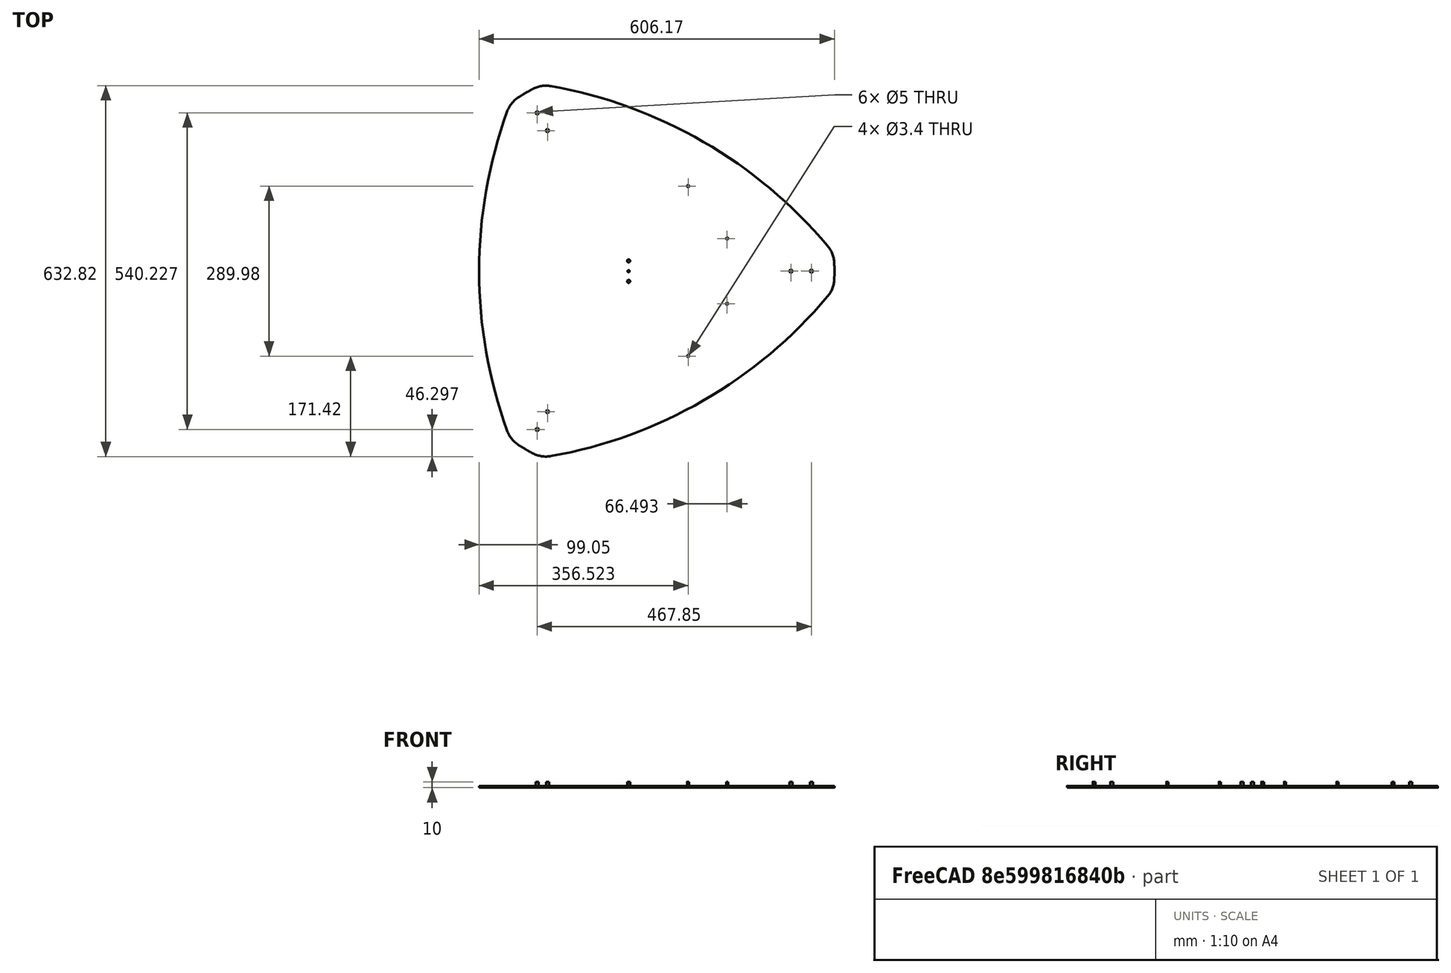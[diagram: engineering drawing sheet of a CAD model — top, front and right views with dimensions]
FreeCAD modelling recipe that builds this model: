
FCSTD DOCUMENT  (FreeCAD 1.1R38827 (Git))
Label: composit_stand3_basement_top_PP_model
License: All rights reserved
LicenseURL: http://en.wikipedia.org/wiki/All_rights_reserved
objects: Part::FeaturePython×7, App::Link×3, PartDesign::SubShapeBinder×2, PartDesign::CoordinateSystem×2, Part::Mirroring×1, Part::Compound×1, Part::Offset2D×1, PartDesign::Pad×1, Part::Cylinder×1, Part::Extrusion×1, Part::MultiFuse×1, PartDesign::Boolean×1, PartDesign::Body×1
note: 23 computed .brp shape members not serialized (recipe doc carries the construction recipe); baked Part::Feature solids carry a one-line shape summary decoded from their .brp
EXTERNAL_REF file=composit_stand3_basement_top_main.FCStd obj=Sketch
EXTERNAL_REF file=composit_stand3_basin_holder_main.FCStd obj=Join
EXTERNAL_REF file=../U-fix.FCStd obj=Sketch002
EXTERNAL_REF file=composit_stand3_base_part1_main.FCStd obj=Placment003

FEATURE [PartDesign::SubShapeBinder] Binder
  BindCopyOnChange = 0
  BindMode = 0
  ClaimChildren = true
  Fuse = false
  MakeFace = true
  OffsetFill = false
  OffsetIntersection = false
  OffsetJoinType = 0
  OffsetOpenResult = false
  PartialLoad = false
  Relative = true
  Support = -> [<external composit_stand3_basement_top_main.FCStd>#Sketch]
  _Version = 2
FEATURE [Part::FeaturePython] PolarArray  # WARN: FeaturePython — macro-defined, semantics opaque (R4)
  Alignment = 0
  AttacherType = Attacher::AttachEngine3D
  CellStart = A1
  Count = 3
  DistributionLaw = 0
  EndInclusive = false
  ExposePlacement = false
  FlipX = false
  FlipZ = false
  GeneratorMode = 0
  MarkerShape = 1
  MarkerSize = 0
  NumElements = 3
  OrientMode = 2
  Radius = 100
  Reverse = false
  SpanEnd = 360
  SpanStart = 0
  Step = 120
  Type = lattice2PolarArray2.PolarArray
  UseArcRadius = false
  UseArcRange = 0
  VSGVersion = 1
  Values = 0.0 | 120.0 | 240.0
  ValuesSource = 2
  isLattice = 1
FEATURE [Part::Mirroring] Part__Mirroring  label="Binder (Mirror #1)"
  Base = (0,0,0)
  Normal = (0,1,0)
  Source = -> Binder
FEATURE [Part::Compound] Compound
  Links = -> [Binder,Part__Mirroring]
FEATURE [Part::FeaturePython] Populate  label="Populate PolarArray with Compound"  # WARN: FeaturePython — macro-defined, semantics opaque (R4)
  Copying = 0
  ExposePlacement = false
  MarkerShape = 1
  MarkerSize = 0
  NumElements = 0
  Object = -> Compound
  OutputCompounding = 1
  PlacementsTo = -> PolarArray
  Referencing = 1
  Type = lattice2PopulateCopies.LatticePopulateCopies
  isLattice = 0
FEATURE [Part::FeaturePython] Connect  # WARN: FeaturePython — macro-defined, semantics opaque (R4)
  Objects = -> [Populate]
  Tolerance = 0
FEATURE [Part::Offset2D] Offset2D
  Fill = false
  Intersection = false
  Join = 0
  Mode = 1
  SelfIntersection = false
  Source = -> Connect
  Value = 2
FEATURE [PartDesign::SubShapeBinder] Binder001
  BindCopyOnChange = 0
  BindMode = 0
  ClaimChildren = true
  Context = -> Body [Binder001.]
  Fuse = false
  MakeFace = true
  OffsetFill = false
  OffsetIntersection = false
  OffsetJoinType = 0
  OffsetOpenResult = false
  PartialLoad = false
  Relative = true
  Support = -> [Offset2D]
  _Version = 2
FEATURE [PartDesign::Pad] Pad
  Direction = (0,0,1)
  Length = 3
  Length2 = 10
  Profile = -> Binder001
  Refine = true
  Suppressed = false
  Type = 0
FEATURE [Part::Cylinder] Cylinder  label="hole_3.4mm"
  Angle = 360
  AttacherType = Attacher::AttachEngine3D
  FirstAngle = 0
  Height = 10
  Radius = 1.7
  SecondAngle = 0
FEATURE [App::Link] Link  label="holes"
  LinkedObject = -> <external composit_stand3_basin_holder_main.FCStd>#Join
FEATURE [Part::FeaturePython] Populate001  label="Populate holes with hole_3.4mm"  # WARN: FeaturePython — macro-defined, semantics opaque (R4)
  Copying = 0
  ExposePlacement = false
  MarkerShape = 1
  MarkerSize = 0
  NumElements = 0
  Object = -> Cylinder
  OutputCompounding = 1
  PlacementsTo = -> Link
  Referencing = 0
  Type = lattice2PopulateCopies.LatticePopulateCopies
  isLattice = 0
FEATURE [PartDesign::CoordinateSystem] Local_CS  label="bottom_LCS"
  AttacherType = Attacher::AttachEngine3D
  AttachmentSupport = -> [XY_Plane]
  MapMode = 5
FEATURE [PartDesign::CoordinateSystem] Local_CS001  label="top_LCS"
  AttacherType = Attacher::AttachEngine3D
  AttachmentOffset = pos=(0,0,3) rot=(0,0,1;0rad)
  AttachmentSupport = -> [XY_Plane]
  MapMode = 5
  Placement = pos=(0,0,3) rot=(0,0,1;0rad)
FEATURE [App::Link] Link001  label="holes_bottom"
  LinkedObject = -> <external ../U-fix.FCStd>#Sketch002
FEATURE [Part::Extrusion] Extrude
  Base = -> Link001
  Dir = (0,0,1)
  DirMode = 2
  FaceMakerClass = Part::FaceMakerBullseye
  FaceMakerMode = 3
  LengthFwd = 10
  LengthRev = 0
  Solid = true
  Symmetric = false
FEATURE [App::Link] Link002  label="bottom_fix_placement"
  LinkTransform = true
  LinkedObject = -> <external composit_stand3_base_part1_main.FCStd>#Placment003
FEATURE [Part::FeaturePython] PolarArray001  # WARN: FeaturePython — macro-defined, semantics opaque (R4)
  Alignment = 0
  AttacherType = Attacher::AttachEngine3D
  CellStart = A1
  Count = 3
  DistributionLaw = 0
  EndInclusive = false
  ExposePlacement = false
  FlipX = false
  FlipZ = false
  GeneratorMode = 0
  MarkerShape = 1
  MarkerSize = 0
  NumElements = 3
  OrientMode = 2
  Radius = 250
  Reverse = false
  SpanEnd = 360
  SpanStart = 0
  Step = 120
  Type = lattice2PolarArray2.PolarArray
  UseArcRadius = false
  UseArcRange = 0
  VSGVersion = 1
  Values = 0.0 | 120.0 | 240.0
  ValuesSource = 2
  isLattice = 1
FEATURE [Part::FeaturePython] Populate002  label="Populate PolarArray001 with bottom_fix_placement"  # WARN: FeaturePython — macro-defined, semantics opaque (R4)
  Copying = 0
  ExposePlacement = false
  MarkerShape = 1
  MarkerSize = 0
  NumElements = 3
  Object = -> Link002
  OutputCompounding = 0
  PlacementsTo = -> PolarArray001
  Referencing = 1
  Type = lattice2PopulateCopies.LatticePopulateCopies
  isLattice = 1
FEATURE [Part::FeaturePython] Populate003  label="Populate Populate PolarArray001 with bottom_fix_placement with Extrude"  # WARN: FeaturePython — macro-defined, semantics opaque (R4)
  Copying = 0
  ExposePlacement = false
  MarkerShape = 1
  MarkerSize = 0
  NumElements = 0
  Object = -> Extrude
  OutputCompounding = 1
  PlacementsTo = -> Populate002
  Referencing = 0
  Type = lattice2PopulateCopies.LatticePopulateCopies
  isLattice = 0
FEATURE [Part::MultiFuse] Fusion
  Shapes = -> [Populate001,Populate003]
FEATURE [PartDesign::Boolean] Boolean
  BaseFeature = -> Pad
  Group = -> [Fusion]
  Suppressed = false
  Type = 1
  UsePlacement = true
FEATURE [PartDesign::Body] Body  label="top_PP"
  AllowCompound = false
  Group = -> [Binder001,Pad,Boolean,Local_CS,Local_CS001]
  Origin = -> Origin
  Tip = -> Boolean

RESOLVED EXTERNAL PARTS (link-assembly join: the EXTERNAL_REF files above that resolve inside this repo's crawl, each included once):
---- part ../U-fix.FCStd = doc fcstd_8b42821c5992 ----
FCSTD DOCUMENT  (FreeCAD 1.1R38827 (Git))
Label: U-fix
License: All rights reserved
LicenseURL: http://en.wikipedia.org/wiki/All_rights_reserved
objects: Sketcher::SketchObject×7, TechDraw::DrawViewDimension×4, TechDraw::DrawViewPart×3, PartDesign::SubShapeBinder×2, PartDesign::Pocket×2, PartDesign::FeaturePython×1, PartDesign::Mirrored×1, TechDraw::DrawSVGTemplate×1, Part::Feature×1, PartDesign::Hole×1, PartDesign::Body×1, TechDraw::DrawPage×1, App::DocumentObjectGroup×1
note: 37 computed .brp shape members not serialized (recipe doc carries the construction recipe); baked Part::Feature solids carry a one-line shape summary decoded from their .brp
EXTERNAL_REF file=ugol90degX40mm.FCStd obj=Binder002
EXTERNAL_REF file=wheel50mm.FCStd obj=Populate001

FEATURE [Sketcher::SketchObject] Sketch
  ArcFitTolerance = 0
  AttachmentSupport = -> [XZ_Plane]
  FullyConstrained = true
  MakeInternals = false
  MapMode = 5
  Placement = pos=(0,0,0) rot=(1,0,0;1.5708rad)
  sketch-geometry (5):
    g0: LineSegment StartX=-11.5 StartY=16 StartZ=0 EndX=-11.5 EndY=0 EndZ=0
    g1: LineSegment StartX=-11.5 StartY=0 StartZ=0 EndX=11.5 EndY=0 EndZ=0
    g2: LineSegment StartX=11.5 StartY=0 StartZ=0 EndX=11.5 EndY=16 EndZ=0
    g3: LineSegment [constr] StartX=11.5 StartY=16 StartZ=0 EndX=-11.5 EndY=16 EndZ=0
    g4: GeomPoint [constr] X=0 Y=8 Z=0
  constraints (13):
    c: Coincident(g0,g1)
    c: Coincident(g1,g2)
    c: Coincident(g2,g3)
    c: Coincident(g3,g0)
    c: Horizontal(g1)
    c: Horizontal(g3)
    c: Vertical(g0)
    c: Vertical(g2)
    c: Symmetric(g1,g0,g4)
    c: PointOnObject(g4,g-2)
    c: PointOnObject(g1,g-1)
    c: DistanceX(g1,g1) = 23  'width'
    c: DistanceY(g2) = 16  'height'
FEATURE [PartDesign::FeaturePython] BaseBend  # WARN: FeaturePython — macro-defined, semantics opaque (R4)
  BendSide = 1
  BendSketch = -> Sketch
  MidPlane = true
  Reverse = false
  Suppressed = false
  length = 65
  radius = 2
  thickness = 1
FEATURE [PartDesign::SubShapeBinder] Binder  label="U-fix_vert_holes"
  BindCopyOnChange = 0
  BindMode = 0
  ClaimChildren = false
  Context = -> Body [Binder.]
  Fuse = false
  MakeFace = true
  OffsetFill = false
  OffsetIntersection = false
  OffsetJoinType = 0
  OffsetOpenResult = false
  PartialLoad = false
  Placement = pos=(0,0,0) rot=(0,0,1;1.5708rad)
  Relative = true
  Support = -> [<external ugol90degX40mm.FCStd>#Binder002]
  _Version = 2
  expr: Support = <<ugol90degX40mm>>#<<vert>>._self
FEATURE [PartDesign::Pocket] Pocket
  BaseFeature = -> BaseBend
  Direction = (1,-2e-16,0)
  Length = 5
  Length2 = 5
  Midplane = true
  Profile = -> Binder
  Suppressed = false
  Type = 1
FEATURE [Sketcher::SketchObject] Sketch001
  ArcFitTolerance = 0
  AttachmentOffset = pos=(32.5,16,0) rot=(0,0,1;0rad)
  AttachmentSupport = -> [YZ_Plane]
  FullyConstrained = true
  MakeInternals = false
  MapMode = 5
  Placement = pos=(0,32.5,16) rot=(0.57735,0.57735,0.57735;2.0944rad)
  expr: .AttachmentOffset.Base.x = BaseBend.length / 2
  expr: .AttachmentOffset.Base.y = Sketch.Constraints.height
  sketch-geometry (3):
    g0: ArcOfCircle CenterX=-5 CenterY=-5 CenterZ=0 NormalX=0 NormalY=0 NormalZ=1 AngleXU=0 Radius=5 StartAngle=0 EndAngle=1.5708
    g1: LineSegment StartX=-9e-16 StartY=-5 StartZ=0 EndX=0 EndY=0 EndZ=0
    g2: LineSegment StartX=0 StartY=0 StartZ=0 EndX=-5.00003 EndY=-4.65468e-11 EndZ=0
  constraints (8):
    c: PointOnObject(g0,g-1)
    c: PointOnObject(g0,g-2)
    c: Coincident(g1,g2)
    c: Coincident(g2,g0)
    c: Tangent(g2,g0)
    c: Tangent(g0,g1) = -1.5708
    c: Coincident(g1,g-1)
    c: Diameter(g0) = 10
FEATURE [PartDesign::Pocket] Pocket001
  BaseFeature = -> Pocket
  Direction = (-1,0,0)
  Length = 5
  Length2 = 5
  Midplane = true
  Profile = -> Sketch001
  ReferenceAxis = -> Sketch001 [N_Axis]
  Suppressed = false
  Type = 1
FEATURE [PartDesign::Mirrored] Mirrored
  BaseFeature = -> Pocket001
  MirrorPlane = -> XZ_Plane
  Originals = -> [Pocket001]
  Suppressed = false
  TransformMode = 0
FEATURE [Sketcher::SketchObject] Sketch002  label="holes_bottom"
  ArcFitTolerance = 0
  AttachmentSupport = -> [XY_Plane]
  FullyConstrained = true
  MakeInternals = false
  MapMode = 5
  sketch-geometry (2):
    g0: Circle CenterX=0 CenterY=17.5 CenterZ=0 NormalX=0 NormalY=0 NormalZ=1 AngleXU=0 Radius=2.5
    g1: Circle CenterX=0 CenterY=-17.5 CenterZ=0 NormalX=0 NormalY=0 NormalZ=1 AngleXU=0 Radius=2.5
  constraints (5):
    c: PointOnObject(g0,g-2)
    c: Symmetric(g1,g0,g-1)
    c: Equal(g1,g0)
    c: Diameter(g1) = 5
    c: DistanceY(g1,g0) = 35
FEATURE [TechDraw::DrawSVGTemplate] Template
  Height = 210
  Orientation = 1
  Template = <path>
  Width = 297
FEATURE [Part::Feature] Unfold
  Placement = pos=(0,0,0) rot=(0,0,1;1.5708rad)
  shape: bbox 53 x 50.85 x 1 mm, 16 faces (baked)
FEATURE [Sketcher::SketchObject] Unfold_Sketch_Outline
  ArcFitTolerance = 0
  FullyConstrained = false
  MakeInternals = false
  sketch-geometry (8):
    g0: ArcOfCircle CenterX=21.5 CenterY=-20.427 CenterZ=0 NormalX=0 NormalY=0 NormalZ=1 AngleXU=4e-16 Radius=5 StartAngle=4.71238 EndAngle=6.28319
    g1: LineSegment StartX=26.5 StartY=20.427 StartZ=0 EndX=26.5 EndY=-20.427 EndZ=0
    g2: ArcOfCircle CenterX=21.5 CenterY=20.427 CenterZ=0 NormalX=0 NormalY=0 NormalZ=1 AngleXU=-4e-16 Radius=5 StartAngle=0 EndAngle=1.5708
    g3: LineSegment StartX=21.5 StartY=25.427 StartZ=0 EndX=-21.5 EndY=25.427 EndZ=0
    g4: ArcOfCircle CenterX=-21.5 CenterY=20.427 CenterZ=0 NormalX=0 NormalY=0 NormalZ=1 AngleXU=-3.14159 Radius=5 StartAngle=4.71238 EndAngle=6.28319
    g5: LineSegment StartX=-26.5 StartY=20.427 StartZ=0 EndX=-26.5 EndY=-20.427 EndZ=0
    g6: ArcOfCircle CenterX=-21.5 CenterY=-20.427 CenterZ=0 NormalX=0 NormalY=0 NormalZ=1 AngleXU=3.14159 Radius=5 StartAngle=0 EndAngle=1.5708
    g7: LineSegment StartX=21.5 StartY=-25.427 StartZ=0 EndX=-21.5 EndY=-25.427 EndZ=0
FEATURE [Sketcher::SketchObject] Unfold_Sketch_Internal
  ArcFitTolerance = 0
  FullyConstrained = false
  MakeInternals = false
  sketch-geometry (6):
    g0: Circle CenterX=17.5 CenterY=0 CenterZ=0 NormalX=0 NormalY=0 NormalZ=1 AngleXU=1.5708 Radius=2.75
    g1: Circle CenterX=-17.5 CenterY=0 CenterZ=0 NormalX=0 NormalY=0 NormalZ=1 AngleXU=1.5708 Radius=2.75
    g2: Circle CenterX=20 CenterY=-19.927 CenterZ=0 NormalX=0 NormalY=0 NormalZ=1 AngleXU=2e-16 Radius=1.7
    g3: Circle CenterX=-20 CenterY=-19.927 CenterZ=0 NormalX=0 NormalY=0 NormalZ=1 AngleXU=2e-16 Radius=1.7
    g4: Circle CenterX=20 CenterY=19.927 CenterZ=0 NormalX=0 NormalY=0 NormalZ=-1 AngleXU=-3.14159 Radius=1.7
    g5: Circle CenterX=-20 CenterY=19.927 CenterZ=0 NormalX=0 NormalY=0 NormalZ=-1 AngleXU=-3.14159 Radius=1.7
FEATURE [Sketcher::SketchObject] Unfold_Sketch_bends
  ArcFitTolerance = 0
  FullyConstrained = false
  MakeInternals = false
  sketch-geometry (2):
    g0: LineSegment StartX=-26.5 StartY=10.4635 StartZ=0 EndX=26.5 EndY=10.4635 EndZ=0
    g1: LineSegment StartX=-26.5 StartY=-10.4635 StartZ=0 EndX=26.5 EndY=-10.4635 EndZ=0
FEATURE [Sketcher::SketchObject] Unfold_Sketch
  ArcFitTolerance = 0
  ExternalGeometry = -> [Unfold_Sketch_bends]
  FullyConstrained = false
  MakeInternals = false
  sketch-geometry (18):
    g0: ArcOfCircle CenterX=21.5 CenterY=-20.427 CenterZ=0 NormalX=0 NormalY=0 NormalZ=1 AngleXU=4e-16 Radius=5 StartAngle=4.71238 EndAngle=6.28319
    g1: LineSegment StartX=21.5 StartY=-25.427 StartZ=0 EndX=-21.5 EndY=-25.427 EndZ=0
    g2: ArcOfCircle CenterX=-21.5 CenterY=-20.427 CenterZ=0 NormalX=0 NormalY=0 NormalZ=1 AngleXU=3.14159 Radius=5 StartAngle=0 EndAngle=1.5708
    g3: ArcOfCircle CenterX=-21.5 CenterY=20.427 CenterZ=0 NormalX=0 NormalY=0 NormalZ=1 AngleXU=-3.14159 Radius=5 StartAngle=4.71238 EndAngle=6.28319
    g4: LineSegment StartX=21.5 StartY=25.427 StartZ=0 EndX=-21.5 EndY=25.427 EndZ=0
    g5: ArcOfCircle CenterX=21.5 CenterY=20.427 CenterZ=0 NormalX=0 NormalY=0 NormalZ=1 AngleXU=-4e-16 Radius=5 StartAngle=0 EndAngle=1.5708
    g6: Circle CenterX=-17.5 CenterY=0 CenterZ=0 NormalX=0 NormalY=0 NormalZ=1 AngleXU=1.5708 Radius=2.75
    g7: Circle CenterX=17.5 CenterY=0 CenterZ=0 NormalX=0 NormalY=0 NormalZ=1 AngleXU=1.5708 Radius=2.75
    g8: Circle CenterX=-20 CenterY=19.927 CenterZ=0 NormalX=0 NormalY=0 NormalZ=-1 AngleXU=-3.14159 Radius=1.7
    g9: Circle CenterX=20 CenterY=19.927 CenterZ=0 NormalX=0 NormalY=0 NormalZ=-1 AngleXU=-3.14159 Radius=1.7
    g10: Circle CenterX=-20 CenterY=-19.927 CenterZ=0 NormalX=0 NormalY=0 NormalZ=1 AngleXU=2e-16 Radius=1.7
    g11: Circle CenterX=20 CenterY=-19.927 CenterZ=0 NormalX=0 NormalY=0 NormalZ=1 AngleXU=2e-16 Radius=1.7
    g12: LineSegment StartX=26.5 StartY=20.427 StartZ=0 EndX=26.5 EndY=-20.427 EndZ=0
    g13: LineSegment StartX=-26.5 StartY=20.427 StartZ=0 EndX=-26.5 EndY=-20.427 EndZ=0
    g14: LineSegment StartX=26.5 StartY=-10.4635 StartZ=0 EndX=24.5 EndY=-10.4635 EndZ=0
    g15: LineSegment StartX=26.5 StartY=10.4635 StartZ=0 EndX=24.5 EndY=10.4635 EndZ=0
    g16: LineSegment StartX=-26.5 StartY=10.4635 StartZ=0 EndX=-24.5 EndY=10.4635 EndZ=0
    g17: LineSegment StartX=-26.5 StartY=-10.4635 StartZ=0 EndX=-24.5 EndY=-10.4635 EndZ=0
  constraints (20):
    c: Coincident(g2,g13)
    c: Coincident(g3,g13)
    c: Coincident(g1,g2)
    c: Coincident(g3,g4)
    c: Coincident(g0,g1)
    c: Coincident(g4,g5)
    c: Coincident(g0,g12)
    c: Coincident(g5,g12)
    c: Coincident(g14,g-4)
    c: Coincident(g15,g-3)
    c: Coincident(g16,g-3)
    c: Coincident(g17,g-4)
    c: PointOnObject(g17,g-4)
    c: PointOnObject(g16,g-3)
    c: PointOnObject(g15,g-3)
    c: PointOnObject(g14,g-4)
    c: Equal(g14,g15)
    c: Equal(g15,g16)
    c: Equal(g16,g17)
    c: Distance(g17) = 2
FEATURE [PartDesign::SubShapeBinder] Binder001
  BindCopyOnChange = 0
  BindMode = 0
  ClaimChildren = false
  Context = -> Body [Binder001.]
  Fuse = false
  MakeFace = true
  OffsetFill = false
  OffsetIntersection = false
  OffsetJoinType = 0
  OffsetOpenResult = false
  PartialLoad = false
  Placement = pos=(0,0,0) rot=(0,0,1;0.785398rad)
  Relative = true
  Support = -> [<external wheel50mm.FCStd>#Populate001]
  _Version = 2
  expr: Support = wheel50mm#<<holes_max>>._self
FEATURE [PartDesign::Hole] Hole
  BaseFeature = -> Mirrored
  CustomThreadClearance = 0
  Depth = 25
  DepthType = 0
  Diameter = 5.5
  DrillForDepth = false
  DrillPoint = 1
  DrillPointAngle = 118
  HoleCutCountersinkAngle = 90
  HoleCutCustomValues = false
  HoleCutDepth = 0
  HoleCutDiameter = 6.1
  HoleCutType = 0
  ModelThread = false
  Profile = -> Binder001
  Reversed = true
  Suppressed = false
  Tapered = false
  TaperedAngle = 90
  ThreadClass = 0
  ThreadDepth = 25
  ThreadDepthType = 0
  ThreadDirection = 0
  ThreadFit = 0
  ThreadSize = 0
  ThreadType = 0
  Threaded = false
  UseCustomThreadClearance = false
FEATURE [PartDesign::Body] Body  label="U_fix_material_0.50ansi"
  AllowCompound = false
  Group = -> [Sketch,BaseBend,Binder,Pocket,Sketch001,Pocket001,Mirrored,Sketch002,Hole,Binder001]
  Origin = -> Origin
  Tip = -> Hole
FEATURE [TechDraw::DrawViewPart] View
  CoarseView = false
  Direction = (0,-1,0)
  Focus = 100
  HardHidden = false
  IsoCount = 0
  IsoHidden = false
  IsoVisible = false
  LockPosition = false
  Perspective = false
  Rotation = 0
  ScaleType = 0
  ScrubCount = 0
  SeamHidden = false
  SeamVisible = true
  SmoothHidden = false
  SmoothVisible = true
  Source = -> [Body]
  X = 69.5
  XDirection = (1,0,0)
  Y = 105
  expr: Y = Template.Height / 2
FEATURE [TechDraw::DrawViewPart] View001
  CoarseView = false
  Direction = (1,0,0)
  Focus = 100
  HardHidden = false
  IsoCount = 0
  IsoHidden = false
  IsoVisible = false
  LockPosition = false
  Perspective = false
  Rotation = 0
  ScaleType = 0
  ScrubCount = 0
  SeamHidden = false
  SeamVisible = true
  SmoothHidden = false
  SmoothVisible = true
  Source = -> [Body]
  X = 226.5
  XDirection = (0,1,-1.19209e-07)
  Y = 105
  expr: Y = Template.Height / 2
FEATURE [TechDraw::DrawViewPart] View002
  CoarseView = false
  Direction = (0,0,1)
  Focus = 100
  HardHidden = false
  IsoCount = 0
  IsoHidden = false
  IsoVisible = false
  LockPosition = false
  Perspective = false
  Rotation = 0
  ScaleType = 0
  ScrubCount = 0
  SeamHidden = false
  SeamVisible = true
  SmoothHidden = false
  SmoothVisible = true
  Source = -> [Body]
  X = 148.5
  XDirection = (1,0,0)
  Y = 105
  expr: Y = Template.Height / 2
FEATURE [TechDraw::DrawViewDimension] Dimension004
  AngleOverride = false
  Arbitrary = false
  ArbitraryTolerances = false
  EqualTolerance = true
  ExtensionAngle = 0
  FormatSpec = R%.2w
  FormatSpecOverTolerance = %+.2w
  FormatSpecUnderTolerance = %+.2w
  Inverted = false
  LineAngle = 0
  LockPosition = false
  MeasureType = 1
  OverTolerance = 0
  References2D = -> [View]
  Rotation = 0
  ScaleType = 0
  TheoreticalExact = false
  Type = 4
  UnderTolerance = 0
  X = -23.1952
  Y = -5.48414
FEATURE [TechDraw::DrawViewDimension] Dimension005
  AngleOverride = false
  Arbitrary = false
  ArbitraryTolerances = false
  EqualTolerance = true
  ExtensionAngle = 0
  FormatSpec = R%.2w
  FormatSpecOverTolerance = %+.2w
  FormatSpecUnderTolerance = %+.2w
  Inverted = false
  LineAngle = 0
  LockPosition = false
  MeasureType = 1
  OverTolerance = 0
  References2D = -> [View]
  Rotation = 0
  ScaleType = 0
  TheoreticalExact = false
  Type = 4
  UnderTolerance = 0
  X = 1.1181
  Y = 3.75976
FEATURE [TechDraw::DrawViewDimension] Dimension
  AngleOverride = false
  Arbitrary = false
  ArbitraryTolerances = false
  BoxCorners = (2) [(-11.5,-8,-1e-07),(11.5,8,1e-07)]
  EqualTolerance = true
  ExtensionAngle = 0
  FormatSpec = %.2w
  FormatSpecOverTolerance = %+.2w
  FormatSpecUnderTolerance = %+.2w
  Inverted = false
  LineAngle = 0
  LockPosition = false
  MeasureType = 1
  OverTolerance = 0
  References2D = -> [View]
  Rotation = 0
  ScaleType = 0
  TheoreticalExact = false
  Type = 1
  UnderTolerance = 0
  X = -0.401552
  Y = 25.4578
FEATURE [TechDraw::DrawViewDimension] Dimension006
  AngleOverride = false
  Arbitrary = false
  ArbitraryTolerances = false
  BoxCorners = (2) [(-11.5,-8,-1e-07),(11.5,8,1e-07)]
  EqualTolerance = true
  ExtensionAngle = 0
  FormatSpec = %.2w
  FormatSpecOverTolerance = %+.2w
  FormatSpecUnderTolerance = %+.2w
  Inverted = false
  LineAngle = 0
  LockPosition = false
  MeasureType = 1
  OverTolerance = 0
  References2D = -> [View]
  Rotation = 0
  ScaleType = 0
  TheoreticalExact = false
  Type = 2
  UnderTolerance = 0
  X = 18.6275
  Y = 2.60039
FEATURE [TechDraw::DrawPage] Page
  KeepUpdated = true
  NextBalloonIndex = 1
  ProjectionType = 0
  Template = -> Template
  Views = -> [View,View001,View002,Dimension004,Dimension005,Dimension,Dimension006]
FEATURE [App::DocumentObjectGroup] Group  label="unfold_Group"
  Group = -> [Page,Unfold,Unfold_Sketch,Unfold_Sketch_Outline,Unfold_Sketch_Internal,Unfold_Sketch_bends]
note: 1 file-system path scrubbed to <path> (originals preserved in the JSON sidecar)
---- part composit_stand3_base_part1_main.FCStd = doc fcstd_83d21d27950e ----
FCSTD DOCUMENT  (FreeCAD 1.1R38827 (Git))
Label: composit_stand3_base_part1_main
License: All rights reserved
LicenseURL: http://en.wikipedia.org/wiki/All_rights_reserved
objects: Part::FeaturePython×32, Sketcher::SketchObject×7, App::Link×5, Part::Extrusion×3, PartDesign::SubShapeBinder×2, Part::MultiFuse×1, Part::Feature×1
note: 53 computed .brp shape members not serialized (recipe doc carries the construction recipe); baked Part::Feature solids carry a one-line shape summary decoded from their .brp
EXTERNAL_REF file=composit_stand3_main.FCStd obj=Sketch
EXTERNAL_REF file=composit_stand3_main.FCStd obj=LinearArray
EXTERNAL_REF file=../module.FCStd obj=Sketch
EXTERNAL_REF file=composit_stand3_sink_main.FCStd obj=Sketch001
EXTERNAL_REF file=composit_stand3_bottom_shield_main.FCStd obj=Placment
EXTERNAL_REF file=composit_stand3_bottom_shield_main.FCStd obj=LinearArray
EXTERNAL_REF file=composit_stand3_sink_main.FCStd obj=Sketch005

FEATURE [PartDesign::SubShapeBinder] Binder
  BindCopyOnChange = 0
  BindMode = 0
  ClaimChildren = true
  Fuse = false
  MakeFace = false
  OffsetFill = false
  OffsetIntersection = false
  OffsetJoinType = 0
  OffsetOpenResult = false
  PartialLoad = false
  Relative = false
  Support = -> [<external composit_stand3_main.FCStd>#Sketch]
  _Version = 2
FEATURE [Sketcher::SketchObject] Sketch
  ArcFitTolerance = 0
  ExternalGeometry = -> [Binder]
  FullyConstrained = true
  MakeInternals = false
  sketch-geometry (2):
    g0: LineSegment StartX=8.37158 StartY=14.5 StartZ=0 EndX=4.90748 EndY=14.5 EndZ=0
    g1: LineSegment StartX=4.90748 StartY=14.5 StartZ=0 EndX=-2.59252 EndY=27.4904 EndZ=0
  constraints (7):
    c: Horizontal(g0)
    c: Coincident(g0,g1)
    c: Angle(g1) = 2.0944
    c: Coincident(g0,g-3)
    c: Distance(g0,g1) = 3
    c: Distance(g1) = 15
    c: DistanceX(g0) = 4.90748  'x_offset'
FEATURE [Part::FeaturePython] LinearArray  # WARN: FeaturePython — macro-defined, semantics opaque (R4)
  Alignment = 0
  CellStart = A1
  Count = 11
  Dir = (0,0,-1)
  DirIsDriven = true
  DistributionLaw = 0
  DrivenProperty = 1
  EndInclusive = true
  ExposePlacement = false
  GeneratorMode = 1
  MarkerShape = 1
  MarkerSize = 0
  NumElements = 11
  OrientMode = 0
  Point = (0,0,0)
  PointIsDriven = true
  Reverse = false
  SpanEnd = 827
  SpanStart = 27
  Step = 80
  Type = lattice2LinearArray.LinearArray
  VSGVersion = 1
  Values = 27.0 | 107.0 | 187.0 | 267.0 | 347.0 | 427.0 | 507.0 | 587.0 | 667.0 | 747.0 | 827.0
  ValuesSource = 2
  isLattice = 1
  expr: SpanEnd = Step * (Count - 1) * 1 mm + SpanStart
FEATURE [App::Link] Link  label="modules_placement_x"
  LinkTransform = true
  LinkedObject = -> <external composit_stand3_main.FCStd>#LinearArray
FEATURE [Part::FeaturePython] Placment  label="top_placement"  # WARN: FeaturePython — macro-defined, semantics opaque (R4)
  AttacherType = Attacher::AttachEngine3D
  ExposePlacement = true
  MarkerShape = 1
  MarkerSize = 200
  NumElements = 1
  Placement = pos=(0,0,1428) rot=(0,0,1;0rad)
  Type = lattice2AttachablePlacement.AttachablePlacement
  isLattice = 1
FEATURE [Part::FeaturePython] Populate  label="Populate modules_placement_x with LinearArray"  # WARN: FeaturePython — macro-defined, semantics opaque (R4)
  Copying = 0
  ExposePlacement = false
  MarkerShape = 1
  MarkerSize = 0
  NumElements = 22
  Object = -> LinearArray
  OutputCompounding = 0
  PlacementsTo = -> Link
  Referencing = 0
  Type = lattice2PopulateCopies.LatticePopulateCopies
  isLattice = 1
FEATURE [Part::FeaturePython] Populate001  label="Populate Placment with Populate modules_placement_x with LinearArray"  # WARN: FeaturePython — macro-defined, semantics opaque (R4)
  Copying = 0
  ExposePlacement = false
  MarkerShape = 1
  MarkerSize = 0
  NumElements = 22
  Object = -> Populate
  OutputCompounding = 0
  PlacementsTo = -> Placment
  Referencing = 0
  Type = lattice2PopulateCopies.LatticePopulateCopies
  isLattice = 1
FEATURE [Part::FeaturePython] Placment001  # WARN: FeaturePython — macro-defined, semantics opaque (R4)
  AttacherType = Attacher::AttachEngine3D
  ExposePlacement = true
  MarkerShape = 1
  MarkerSize = 50
  NumElements = 1
  Placement = pos=(0,0,0) rot=(0,0.707107,0.707107;3.14159rad)
  Type = lattice2AttachablePlacement.AttachablePlacement
  isLattice = 1
FEATURE [Part::FeaturePython] Populate002  label="Populate Populate Placment with Populate modules_placement_x with LinearArray with Placment001"  # WARN: FeaturePython — macro-defined, semantics opaque (R4)
  Copying = 0
  ExposePlacement = false
  MarkerShape = 1
  MarkerSize = 0
  NumElements = 22
  Object = -> Placment001
  OutputCompounding = 0
  PlacementsTo = -> Populate001
  Referencing = 0
  Type = lattice2PopulateCopies.LatticePopulateCopies
  isLattice = 1
FEATURE [Part::FeaturePython] Placment002  label="sink_placement"  # WARN: FeaturePython — macro-defined, semantics opaque (R4)
  AttacherType = Attacher::AttachEngine3D
  ExposePlacement = true
  MarkerShape = 1
  MarkerSize = 50
  NumElements = 1
  Placement = pos=(8.37158,14.5,410) rot=(0,0,1;1.0472rad)
  Type = lattice2AttachablePlacement.AttachablePlacement
  isLattice = 1
  expr: .Placement.Base.x = <<composit_stand3_main>>#<<main_sketch>>.Constraints.end_width / 2 / tan(60)
  expr: .Placement.Base.y = <<composit_stand3_main>>#<<main_sketch>>.Constraints.end_width / 2
FEATURE [App::Link] Link001  label="module_holes"
  LinkedObject = -> <external ../module.FCStd>#Sketch
FEATURE [Sketcher::SketchObject] Sketch001  label="basin_cut_top_sketch"
  ArcFitTolerance = 0
  FullyConstrained = true
  MakeInternals = false
  Placement = pos=(0,0,400) rot=(1,0,0;1.5708rad)
  expr: .Placement.Base.z = <<basin_cut_sketch>>.Constraints.height
  expr: Constraints[26] = <<basin_cut_sketch>>.Constraints.length
  expr: Constraints[28] = <<composit_stand3_main>>#<<main_sketch>>.Constraints.x_face_offset + 0.5 mm
  expr: Constraints[30] = <<composit_stand3_sink_main>>#<<side_bottom_edge>>.Constraints.angle
  sketch-geometry (14):
    g0: ArcOfEllipse CenterX=8.87158 CenterY=5 CenterZ=0 NormalX=0 NormalY=0 NormalZ=1 MajorRadius=40 MinorRadius=15 AngleXU=1.5708 StartAngle=4.71239 EndAngle=6.28319
    g1: LineSegment [constr] StartX=8.87158 StartY=45 StartZ=0 EndX=8.87158 EndY=-35 EndZ=0
    g2: LineSegment [constr] StartX=-6.12842 StartY=5 StartZ=0 EndX=23.8716 EndY=5 EndZ=0
    g3: GeomPoint [constr] X=8.87158 Y=42.081 Z=0
    g4: GeomPoint [constr] X=8.87158 Y=-32.081 Z=0
    g5: ArcOfCircle CenterX=28.8716 CenterY=5 CenterZ=0 NormalX=0 NormalY=0 NormalZ=1 AngleXU=0 Radius=5 StartAngle=3.14159 EndAngle=4.71239
    g6: LineSegment StartX=28.8716 StartY=0 StartZ=0 EndX=0 EndY=0 EndZ=0
    g7: LineSegment StartX=0 StartY=0 StartZ=0 EndX=0 EndY=45 EndZ=0
    g8: LineSegment StartX=0 StartY=45 StartZ=0 EndX=8.87158 EndY=45 EndZ=0
    g9: LineSegment StartX=238.446 StartY=3.98838 StartZ=0 EndX=238.446 EndY=0 EndZ=0
    g10: LineSegment StartX=238.446 StartY=0 StartZ=0 EndX=170.25 EndY=0 EndZ=0
    g11: LineSegment StartX=170.836 StartY=0.0172058 StartZ=0 EndX=238.446 EndY=3.98838 EndZ=0
    g12: ArcOfCircle CenterX=170.25 CenterY=10 CenterZ=0 NormalX=0 NormalY=0 NormalZ=1 AngleXU=0 Radius=10 StartAngle=4.71239 EndAngle=4.77106
    g13: LineSegment [constr] StartX=0 StartY=0 StartZ=0 EndX=238.446 EndY=14.0056 EndZ=0
  constraints (31):
    c: InternalAlignment(g1-g4 -> g0) x4
    c: Horizontal(g2)
    c: PointOnObject(g5,g-1)
    c: Tangent(g5,g0) = 1.5708
    c: Coincident(g6,g7)
    c: PointOnObject(g7,g-2)
    c: Vertical(g7)
    c: Coincident(g7,g8)
    c: Horizontal(g8)
    c: Tangent(g8,g0) = 1.5708
    c: Radius(g5) = 5
    c: Tangent(g5,g6) = 1.5708
    c: Horizontal(g6)
    c: DistanceY(g7) = 45  'sink_cut_height'
    c: Horizontal(g0,g0)
    c: DistanceX(g2,g2) = 30
    c: PointOnObject(g10,g-1)
    c: Coincident(g11,g9)
    c: PointOnObject(g9,g-1)
    c: Vertical(g9)
    c: Coincident(g9,g10)
    c: Tangent(g12,g10) = 1.5708
    c: Tangent(g12,g11) = -1.5708
    c: DistanceX(g9) = 238.446
    c: Radius(g12) = 10
    c: DistanceX(g0) = 8.87158
    c: Coincident(g13,g6)
    c: Angle(g13) = 0.0586697
    c: Vertical(g9,g13)
    c: Parallel(g11,g13)
    c: Distance(g9,g13) = 10
FEATURE [Part::FeaturePython] Placment003  label="bottom_fix_placement"  # WARN: FeaturePython — macro-defined, semantics opaque (R4)
  AttacherType = Attacher::AttachEngine3D
  AttachmentOffset = pos=(0,0,0) rot=(0,0,1;1.5708rad)
  ExposePlacement = true
  MarkerShape = 1
  MarkerSize = 50
  NumElements = 1
  Placement = pos=(294.4,0,0) rot=(0,0,1;1.5708rad)
  Type = lattice2AttachablePlacement.AttachablePlacement
  isLattice = 1
FEATURE [Sketcher::SketchObject] Sketch002  label="leg_amplifier"
  ArcFitTolerance = 0
  ExternalGeometry = -> [Binder]
  FullyConstrained = true
  MakeInternals = false
  Placement = pos=(238.046,0,0) rot=(0,0,1;0rad)
  expr: .Placement.Base.x = <<basin_cut_sketch>>.Constraints.length - 0.4 mm
  sketch-geometry (5):
    g0: LineSegment StartX=10 StartY=-14.5 StartZ=0 EndX=0 EndY=-14.5 EndZ=0
    g1: LineSegment StartX=0 StartY=-14.5 StartZ=0 EndX=0 EndY=11.5 EndZ=0
    g2: LineSegment StartX=0 StartY=11.5 StartZ=0 EndX=15 EndY=11.5 EndZ=0
    g3: LineSegment [constr] StartX=113.826 StartY=14.5 StartZ=0 EndX=113.826 EndY=0 EndZ=0
    g4: LineSegment [constr] StartX=113.826 StartY=0 StartZ=0 EndX=113.826 EndY=-14.5 EndZ=0
  constraints (16):
    c: Horizontal(g0)
    c: Coincident(g0,g1)
    c: Vertical(g1)
    c: Coincident(g1,g2)
    c: Horizontal(g2)
    c: DistanceY(g1,g-3) = 3
    c: Coincident(g-3,g3)
    c: PointOnObject(g3,g-1)
    c: Vertical(g3)
    c: Coincident(g3,g4)
    c: Vertical(g4)
    c: Equal(g4,g3)
    c: Horizontal(g4,g0)
    c: DistanceX(g2,g2) = 15
    c: DistanceX(g0,g0) = 10
    c: PointOnObject(g-1,g1)
FEATURE [Part::FeaturePython] LinearArray001  # WARN: FeaturePython — macro-defined, semantics opaque (R4)
  Alignment = 0
  CellStart = A1
  Count = 5
  Dir = (1,0,0)
  DirIsDriven = true
  DistributionLaw = 0
  DrivenProperty = 1
  EndInclusive = true
  ExposePlacement = false
  GeneratorMode = 0
  MarkerShape = 1
  MarkerSize = 0
  NumElements = 5
  OrientMode = 1
  Point = (0,0,0)
  PointIsDriven = true
  Reverse = false
  SpanEnd = 50
  SpanStart = 0
  Step = 12.5
  Type = lattice2LinearArray.LinearArray
  VSGVersion = 1
  Values = 0.0 | 12.5 | 25.0 | 37.5 | 50.0
  ValuesSource = 2
  isLattice = 1
FEATURE [Part::FeaturePython] Placment004  # WARN: FeaturePython — macro-defined, semantics opaque (R4)
  AttacherType = Attacher::AttachEngine3D
  AttachmentOffset = pos=(-3,261,7) rot=(-0.57735,-0.57735,0.57735;2.0944rad)
  AttachmentSupport = -> [Sketch]
  ExposePlacement = true
  MapMode = 7
  MarkerShape = 1
  MarkerSize = 5
  NumElements = 1
  Placement = pos=(-1.6906,19.9282,261) rot=(0.250563,-0.935113,0.250563;1.63783rad)
  Type = lattice2AttachablePlacement.AttachablePlacement
  isLattice = 1
FEATURE [Part::FeaturePython] Populate004  label="Populate Placment004 with LinearArray001"  # WARN: FeaturePython — macro-defined, semantics opaque (R4)
  Copying = 0
  ExposePlacement = false
  MarkerShape = 1
  MarkerSize = 0
  NumElements = 5
  Object = -> LinearArray001
  OutputCompounding = 0
  PlacementsTo = -> Placment004
  Referencing = 0
  Type = lattice2PopulateCopies.LatticePopulateCopies
  isLattice = 1
FEATURE [Sketcher::SketchObject] Sketch003  label="basin_cut_sketch"
  ArcFitTolerance = 0
  FullyConstrained = true
  MakeInternals = false
  Placement = pos=(0,0,0) rot=(1,0,0;1.5708rad)
  expr: .Constraints.length = 206.5 / sin(60)
  sketch-geometry (4):
    g0: LineSegment StartX=0 StartY=0 StartZ=0 EndX=238.446 EndY=0 EndZ=0
    g1: LineSegment StartX=238.446 StartY=0 StartZ=0 EndX=238.446 EndY=400 EndZ=0
    g2: LineSegment StartX=238.446 StartY=400 StartZ=0 EndX=0 EndY=400 EndZ=0
    g3: LineSegment StartX=0 StartY=400 StartZ=0 EndX=0 EndY=0 EndZ=0
  constraints (11):
    c: Coincident(g0,g1)
    c: Coincident(g1,g2)
    c: Coincident(g2,g3)
    c: Coincident(g3,g0)
    c: Horizontal(g0)
    c: Horizontal(g2)
    c: Vertical(g1)
    c: Vertical(g3)
    c: Coincident(g0,g-1)
    c: DistanceY(g3,g3) = 400  'height'
    c: DistanceX(g0,g0) = 238.446  'length'
FEATURE [Part::Extrusion] Extrude001
  Base = -> Sketch003
  Dir = (0,-1,2e-16)
  DirMode = 2
  FaceMakerClass = Part::FaceMakerBullseye
  FaceMakerMode = 3
  LengthFwd = 29
  LengthRev = 0
  Solid = true
  Symmetric = true
  expr: LengthFwd = <<composit_stand3_main>>#<<main_sketch>>.Constraints.end_width
FEATURE [Part::Extrusion] Extrude002
  Base = -> Sketch001
  Dir = (0,-1,2e-16)
  DirMode = 2
  FaceMakerClass = Part::FaceMakerBullseye
  FaceMakerMode = 3
  LengthFwd = 29
  LengthRev = 0
  Solid = true
  Symmetric = true
  expr: LengthFwd = <<Extrude001>>.LengthFwd
FEATURE [Part::MultiFuse] Fusion  label="basin_cut"
  Refine = true
  Shapes = -> [Extrude001,Extrude002]
FEATURE [Sketcher::SketchObject] Sketch004
  ArcFitTolerance = 0
  FullyConstrained = true
  MakeInternals = false
  Placement = pos=(8.37158,14.5,0) rot=(0.774597,-0.447214,-0.447214;1.82348rad)
  expr: .Placement.Base.x = composit_stand3_main#<<main_sketch>>.Constraints.x_face_offset
  expr: Constraints[9] = <<basin_cut_sketch>>.Constraints.height + <<basin_cut_top_sketch>>.Constraints.sink_cut_height
  sketch-geometry (4):
    g0: LineSegment StartX=0 StartY=0 StartZ=0 EndX=0 EndY=445 EndZ=0
    g1: LineSegment StartX=0 StartY=445 StartZ=0 EndX=-1 EndY=445 EndZ=0
    g2: LineSegment StartX=-1 StartY=445 StartZ=0 EndX=-1 EndY=0 EndZ=0
    g3: LineSegment StartX=-1 StartY=0 StartZ=0 EndX=0 EndY=0 EndZ=0
  constraints (11):
    c: Coincident(g0,g1)
    c: Coincident(g1,g2)
    c: Coincident(g2,g3)
    c: Coincident(g3,g0)
    c: Vertical(g0)
    c: Vertical(g2)
    c: Horizontal(g1)
    c: Horizontal(g3)
    c: Coincident(g0,g-1)
    c: DistanceY(g0,g0) = 445
    c: DistanceX(g3,g3) = 1
FEATURE [Part::Extrusion] Extrude003
  Base = -> Sketch004
  Dir = (-0.866025,-0.5,2e-16)
  DirMode = 2
  FaceMakerClass = Part::FaceMakerBullseye
  FaceMakerMode = 3
  LengthFwd = 10
  LengthRev = 0
  Solid = true
  Symmetric = false
FEATURE [App::Link] Link002  label="edge_placement"
  LinkTransform = true
  LinkedObject = -> <external composit_stand3_bottom_shield_main.FCStd>#Placment
FEATURE [App::Link] Link003  label="fix_placements"
  LinkTransform = true
  LinkedObject = -> <external composit_stand3_bottom_shield_main.FCStd>#LinearArray
FEATURE [Sketcher::SketchObject] Sketch005  label="shield_fix_hole_sketch"
  ArcFitTolerance = 0
  FullyConstrained = true
  MakeInternals = false
  sketch-geometry (5):
    g0: LineSegment StartX=-3.2 StartY=-26.4022 StartZ=0 EndX=0 EndY=-26.4022 EndZ=0
    g1: LineSegment StartX=0 StartY=-26.4022 StartZ=0 EndX=0 EndY=26.4022 EndZ=0
    g2: LineSegment StartX=0 StartY=26.4022 StartZ=0 EndX=-3.2 EndY=26.4022 EndZ=0
    g3: LineSegment StartX=-3.2 StartY=26.4022 StartZ=0 EndX=-3.2 EndY=-26.4022 EndZ=0
    g4: GeomPoint [constr] X=-1.6 Y=0 Z=0
  constraints (13):
    c: Coincident(g0,g1)
    c: Coincident(g1,g2)
    c: Coincident(g2,g3)
    c: Coincident(g3,g0)
    c: Horizontal(g0)
    c: Horizontal(g2)
    c: Vertical(g1)
    c: Vertical(g3)
    c: Symmetric(g2,g0,g4)
    c: PointOnObject(g4,g-1)
    c: PointOnObject(g1,g-2)
    c: DistanceX(g0,g1) = 3.2
    c: DistanceY(g0,g1) = 52.8044
FEATURE [Part::FeaturePython] Placment005  label="shield_placement"  # WARN: FeaturePython — macro-defined, semantics opaque (R4)
  AttacherType = Attacher::AttachEngine3D
  ExposePlacement = true
  MarkerShape = 1
  MarkerSize = 50
  NumElements = 1
  Placement = pos=(0,0,0) rot=(0,0,1;1.0472rad)
  Type = lattice2AttachablePlacement.AttachablePlacement
  isLattice = 1
FEATURE [Part::FeaturePython] Placment006  label="Custom"  # WARN: FeaturePython — macro-defined, semantics opaque (R4)
  ExposePlacement = true
  FlipZ = false
  Invert = false
  MarkerShape = 1
  MarkerSize = 50
  NumElements = 1
  Placement = pos=(0,0,0) rot=(0.774597,0.447214,0.447214;1.82348rad)
  PlacementChoice = 0
  Type = lattice2Placement.LatticePlacement
  isLattice = 1
FEATURE [Part::FeaturePython] Populate008  label="Populate edge_placement with fix_placements"  # WARN: FeaturePython — macro-defined, semantics opaque (R4)
  Copying = 0
  ExposePlacement = false
  MarkerShape = 1
  MarkerSize = 0
  NumElements = 4
  Object = -> Link003
  OutputCompounding = 0
  PlacementsTo = -> Link002
  Referencing = 0
  Type = lattice2PopulateCopies.LatticePopulateCopies
  isLattice = 1
FEATURE [Part::FeaturePython] Populate009  label="Populate Populate edge_placement with fix_placements with Custom"  # WARN: FeaturePython — macro-defined, semantics opaque (R4)
  Copying = 0
  ExposePlacement = false
  MarkerShape = 1
  MarkerSize = 0
  NumElements = 4
  Object = -> Placment006
  OutputCompounding = 0
  PlacementsTo = -> Populate008
  Referencing = 0
  Type = lattice2PopulateCopies.LatticePopulateCopies
  isLattice = 1
FEATURE [Part::FeaturePython] Mirror002  label="Mirror002 of Populate Populate edge_placement with fix_placements with Custom"  # WARN: FeaturePython — macro-defined, semantics opaque (R4)
  ExposePlacement = false
  FlipX = false
  FlipY = true
  FlipZ = false
  MarkerShape = 1
  MarkerSize = 0
  NumElements = 4
  Object = -> Populate009
  ObjectTraversal = 0
  Type = lattice2Mirror.LatticeMirror
  isLattice = 1
FEATURE [Part::FeaturePython] Populate011  label="Populate shield_placement with Mirror002 of Populate Populate edge_placement with fix_placements with Custom"  # WARN: FeaturePython — macro-defined, semantics opaque (R4)
  Copying = 0
  ExposePlacement = false
  MarkerShape = 1
  MarkerSize = 0
  NumElements = 4
  Object = -> Mirror002
  OutputCompounding = 0
  PlacementsTo = -> Placment005
  Referencing = 0
  Type = lattice2PopulateCopies.LatticePopulateCopies
  isLattice = 1
FEATURE [Part::FeaturePython] Join002  label="shield_fix_holes"  # WARN: FeaturePython — macro-defined, semantics opaque (R4)
  ExposePlacement = false
  Interleave = false
  Links = -> [Populate011]
  MarkerShape = 1
  MarkerSize = 0
  NumElements = 4
  Type = lattice2JoinArrays.JoinArrays
  isLattice = 1
FEATURE [Part::FeaturePython] LinearArray002  label="leg_fix_placements"  # WARN: FeaturePython — macro-defined, semantics opaque (R4)
  Alignment = 0
  CellStart = A1
  Count = 3
  Dir = (1,0,0)
  DirIsDriven = true
  DistributionLaw = 0
  DrivenProperty = 1
  EndInclusive = true
  ExposePlacement = false
  GeneratorMode = 0
  MarkerShape = 1
  MarkerSize = 0
  NumElements = 3
  OrientMode = 1
  Placement = pos=(245,14.5,0) rot=(0.57735,0.57735,0.57735;4.18879rad)
  Point = (0,0,0)
  PointIsDriven = true
  Reverse = false
  SpanEnd = 390
  SpanStart = 20
  Step = 185
  Type = lattice2LinearArray.LinearArray
  VSGVersion = 1
  Values = 20.0 | 205.0 | 390.0
  ValuesSource = 2
  isLattice = 1
  expr: .Placement.Base.y = <<composit_stand3_main>>#<<main_sketch>>.Constraints.end_width / 2
FEATURE [Part::FeaturePython] Placment007  # WARN: FeaturePython — macro-defined, semantics opaque (R4)
  AttacherType = Attacher::AttachEngine3D
  AttachmentOffset = pos=(3,0,4.42) rot=(0.57735,0.57735,0.57735;2.0944rad)
  AttachmentSupport = -> [Sketch]
  ExposePlacement = true
  MapMode = 7
  MarkerShape = 1
  MarkerSize = 20
  NumElements = 1
  Placement = pos=(2.21555,25.1625,0) rot=(0.694747,0.186157,0.694747;3.50969rad)
  Type = lattice2AttachablePlacement.AttachablePlacement
  isLattice = 1
FEATURE [Part::FeaturePython] Placment008  label="magnet_fix_placement"  # WARN: FeaturePython — macro-defined, semantics opaque (R4)
  AttacherType = Attacher::AttachEngine3D
  ExposePlacement = true
  MarkerShape = 1
  MarkerSize = 50
  NumElements = 1
  Placement = pos=(308.872,-14.5,248) rot=(1,0,0;1.5708rad)
  Type = lattice2AttachablePlacement.AttachablePlacement
  isLattice = 1
  expr: .Placement.Base.x = 300.5 mm + <<composit_stand3_main>>#<<main_sketch>>.Constraints.x_face_offset
  expr: .Placement.Base.y = -<<composit_stand3_main>>#<<main_sketch>>.Constraints.end_width / 2
FEATURE [Part::Feature] Body159  label="part1_material_0.30ansi002"
  Placement = pos=(0,0,0) rot=(0,0,-1;1.5708rad)
  shape: bbox 356 x 59.31 x 1428 mm, 498 faces (baked)
FEATURE [Part::FeaturePython] LinearArray003  # WARN: FeaturePython — macro-defined, semantics opaque (R4)
  Alignment = 0
  CellStart = A1
  Count = 5
  Dir = (1,0,0)
  DirIsDriven = true
  DistributionLaw = 0
  DrivenProperty = 1
  EndInclusive = true
  ExposePlacement = false
  GeneratorMode = 0
  MarkerShape = 1
  MarkerSize = 0
  NumElements = 5
  OrientMode = 1
  Point = (0,0,0)
  PointIsDriven = true
  Reverse = false
  SpanEnd = 1343
  SpanStart = 523
  Step = 205
  Type = lattice2LinearArray.LinearArray
  VSGVersion = 1
  Values = 523.0 | 728.0 | 933.0 | 1138.0 | 1343.0
  ValuesSource = 2
  isLattice = 1
FEATURE [Part::FeaturePython] Populate012  label="parts_fix_holes"  # WARN: FeaturePython — macro-defined, semantics opaque (R4)
  Copying = 0
  ExposePlacement = false
  MarkerShape = 1
  MarkerSize = 0
  NumElements = 5
  Object = -> LinearArray003
  OutputCompounding = 0
  PlacementsTo = -> Placment007
  Referencing = 0
  Type = lattice2PopulateCopies.LatticePopulateCopies
  isLattice = 1
FEATURE [Part::FeaturePython] Placment009  # WARN: FeaturePython — macro-defined, semantics opaque (R4)
  AttacherType = Attacher::AttachEngine3D
  ExposePlacement = true
  MarkerShape = 1
  MarkerSize = 20
  NumElements = 1
  Placement = pos=(181.372,0,0) rot=(0,0,1;0rad)
  Type = lattice2AttachablePlacement.AttachablePlacement
  isLattice = 1
  expr: .Placement.Base.x = <<modules_placement_x>>.LinkedObject.Placement.Base.x * 1 mm + (<<modules_placement_x>>.LinkedObject.SpanStart + <<modules_placement_x>>.LinkedObject.SpanEnd) / 2
FEATURE [Part::FeaturePython] PolarArray  # WARN: FeaturePython — macro-defined, semantics opaque (R4)
  Alignment = 0
  AttacherType = Attacher::AttachEngine3D
  CellStart = A1
  Count = 2
  DistributionLaw = 0
  EndInclusive = false
  ExposePlacement = false
  FlipX = false
  FlipZ = false
  GeneratorMode = 0
  MarkerShape = 1
  MarkerSize = 50
  NumElements = 2
  OrientMode = 2
  Radius = 0
  Reverse = false
  SpanEnd = 360
  SpanStart = 0
  Step = 180
  Type = lattice2PolarArray2.PolarArray
  UseArcRadius = false
  UseArcRange = 0
  VSGVersion = 1
  Values = 0.0 | 180.0
  ValuesSource = 2
  isLattice = 1
FEATURE [Part::FeaturePython] Populate013  label="Populate PolarArray with Populate Populate Placment with Populate modules_placement_x with LinearArray with Placment001"  # WARN: FeaturePython — macro-defined, semantics opaque (R4)
  Copying = 0
  ExposePlacement = false
  MarkerShape = 1
  MarkerSize = 0
  NumElements = 44
  Object = -> Populate002
  OutputCompounding = 0
  PlacementsFrom = -> Placment009
  PlacementsTo = -> PolarArray
  Referencing = 3
  Type = lattice2PopulateCopies.LatticePopulateCopies
  isLattice = 1
FEATURE [Part::FeaturePython] Populate014  label="Populate Placment009 with Populate PolarArray with Populate Populate Placment with Populate modules_placement_x with LinearArray with Placment001"  # WARN: FeaturePython — macro-defined, semantics opaque (R4)
  Copying = 0
  ExposePlacement = false
  MarkerShape = 1
  MarkerSize = 0
  NumElements = 44
  Object = -> Populate013
  OutputCompounding = 0
  PlacementsTo = -> Placment009
  Referencing = 0
  Type = lattice2PopulateCopies.LatticePopulateCopies
  isLattice = 1
FEATURE [Part::FeaturePython] Join  label="modules_placements"  # WARN: FeaturePython — macro-defined, semantics opaque (R4)
  ExposePlacement = false
  Interleave = false
  Links = -> [Populate014]
  MarkerShape = 1
  MarkerSize = 0
  NumElements = 44
  Type = lattice2JoinArrays.JoinArrays
  isLattice = 1
FEATURE [App::Link] Link004  label="side_holes_half_sketch"
  LinkTransform = true
  LinkedObject = -> <external composit_stand3_sink_main.FCStd>#Sketch005
FEATURE [PartDesign::SubShapeBinder] Binder001
  BindCopyOnChange = 0
  BindMode = 0
  ClaimChildren = false
  Fuse = false
  MakeFace = true
  OffsetFill = false
  OffsetIntersection = false
  OffsetJoinType = 0
  OffsetOpenResult = false
  PartialLoad = false
  Relative = true
  Support = -> [Link004]
  _Version = 2
FEATURE [Sketcher::SketchObject] Sketch006
  ArcFitTolerance = 1e-06
  ExternalGeometry = -> [Binder001]
  FullyConstrained = true
  MakeInternals = false
  Placement = pos=(0,0,0) rot=(0.774597,0.447214,0.447214;1.82348rad)
  sketch-geometry (6):
    g0: Circle CenterX=13.8756 CenterY=84 CenterZ=0 NormalX=0 NormalY=0 NormalZ=1 AngleXU=0 Radius=1.7
    g1: Circle CenterX=173.002 CenterY=84 CenterZ=0 NormalX=0 NormalY=0 NormalZ=1 AngleXU=0 Radius=1.7
    g2: Circle CenterX=332.128 CenterY=84 CenterZ=0 NormalX=0 NormalY=0 NormalZ=1 AngleXU=0 Radius=1.7
    g3: Circle CenterX=332.128 CenterY=34 CenterZ=0 NormalX=0 NormalY=0 NormalZ=1 AngleXU=0 Radius=1.7
    g4: LineSegment [constr] StartX=13.8756 StartY=84 StartZ=0 EndX=14.3756 EndY=84 EndZ=0
    g5: LineSegment [constr] StartX=331.628 StartY=84 StartZ=0 EndX=332.128 EndY=84 EndZ=0
  constraints (15):
    c: Symmetric(g0,g2,g1)
    c: Horizontal(g0,g2)
    c: Coincident(g4,g0)
    c: Coincident(g4,g-3)
    c: Coincident(g5,g-4)
    c: Coincident(g5,g2)
    c: Equal(g4,g5)
    c: DistanceX(g4,g4) = 0.5
    c: Equal(g3,g2)
    c: Equal(g3,g1)
    c: Equal(g3,g0)
    c: Diameter(g3) = 3.4
    c: Horizontal(g4)
    c: Horizontal(g3,g-5)
    c: Vertical(g3,g2)
FEATURE [Part::FeaturePython] Downgrade  label="Edges of Sketch006"  # WARN: FeaturePython — macro-defined, semantics opaque (R4)
  Base = -> Sketch006
  Mode = 8
FEATURE [Part::FeaturePython] ArrayFromShape  label="Array from Edges of Sketch006"  # WARN: FeaturePython — macro-defined, semantics opaque (R4)
  CompoundTraversal = 1
  ExposePlacement = false
  MarkerShape = 1
  MarkerSize = 20
  NumElements = 4
  OrientElementIndex = 0
  OrientMode = 2
  ShapeLink = -> Downgrade
  TranslateElementIndex = 0
  TranslateMode = 3
  Type = lattice2ArrayFromShape.LatticeArrayFromShape
  isLattice = 1
FEATURE [Part::FeaturePython] Mirror  label="Mirror of Array from Edges of Sketch006"  # WARN: FeaturePython — macro-defined, semantics opaque (R4)
  ExposePlacement = false
  FlipX = false
  FlipY = true
  FlipZ = false
  MarkerShape = 1
  MarkerSize = 0
  NumElements = 4
  Object = -> ArrayFromShape
  ObjectTraversal = 0
  Type = lattice2Mirror.LatticeMirror
  isLattice = 1
FEATURE [Part::FeaturePython] Join003  label="sink_holes"  # WARN: FeaturePython — macro-defined, semantics opaque (R4)
  ExposePlacement = false
  Interleave = false
  Links = -> [ArrayFromShape,Mirror]
  MarkerShape = 1
  MarkerSize = 0
  NumElements = 8
  Type = lattice2JoinArrays.JoinArrays
  isLattice = 1
---- part composit_stand3_basement_top_main.FCStd = doc fcstd_f4f307a48eaa ----
FCSTD DOCUMENT  (FreeCAD 1.1R38827 (Git))
Label: composit_stand3_basement_top_main
License: All rights reserved
LicenseURL: http://en.wikipedia.org/wiki/All_rights_reserved
objects: Sketcher::SketchObject×1
note: 2 computed .brp shape members not serialized (recipe doc carries the construction recipe); baked Part::Feature solids carry a one-line shape summary decoded from their .brp

FEATURE [Sketcher::SketchObject] Sketch  label="basement_top_main_sketch"
  ArcFitTolerance = 0
  FullyConstrained = true
  MakeInternals = false
  sketch-geometry (4):
    g0: LineSegment [constr] StartX=0 StartY=0 StartZ=0 EndX=126.5 EndY=219.104 EndZ=0
    g1: ArcOfCircle CenterX=0 CenterY=0 CenterZ=0 NormalX=0 NormalY=0 NormalZ=1 AngleXU=0 Radius=349.171 StartAngle=0 EndAngle=0.0396574
    g2: ArcOfCircle CenterX=302.433 CenterY=12 CenterZ=0 NormalX=0 NormalY=0 NormalZ=1 AngleXU=0 Radius=46.5 StartAngle=0.0396574 EndAngle=0.699903
    g3: ArcOfCircle CenterX=-272.703 CenterY=-472.335 CenterZ=0 NormalX=0 NormalY=0 NormalZ=1 AngleXU=0 Radius=798.406 StartAngle=0.699903 EndAngle=1.0472
  constraints (12):
    c: Coincident(g0,g-1)
    c: Angle(g0) = 1.0472
    c: Coincident(g1,g0)
    c: PointOnObject(g1,g-1)
    c: Coincident(g3,g0)
    c: Tangent(g2,g1) = -1.5708
    c: Tangent(g3,g2) = -1.5708
    c: Perpendicular(g3,g0)
    c: DistanceX(g1) = 349.171  'max_r'
    c: Distance(g0) = 253  'min_r'
    c: Radius(g2) = 46.5
    c: DistanceY(g2) = 12
---- part composit_stand3_basin_holder_main.FCStd = doc fcstd_00614ada5c51 ----
FCSTD DOCUMENT  (FreeCAD 1.1R38827 (Git))
Label: composit_stand3_basin_holder_main
License: All rights reserved
LicenseURL: http://en.wikipedia.org/wiki/All_rights_reserved
objects: Part::FeaturePython×2, Sketcher::SketchObject×1
note: 4 computed .brp shape members not serialized (recipe doc carries the construction recipe); baked Part::Feature solids carry a one-line shape summary decoded from their .brp
EXTERNAL_REF file=../basin_big.FCStd obj=Spreadsheet

FEATURE [Sketcher::SketchObject] Sketch  label="main_sketch"
  ArcFitTolerance = 0
  FullyConstrained = true
  MakeInternals = false
  expr: .Constraints.min_r = <<basin_big>>#<<Properties>>.bottom_d / 2 + 10 mm
  sketch-geometry (5):
    g0: ArcOfCircle CenterX=0 CenterY=0 CenterZ=0 NormalX=0 NormalY=0 NormalZ=1 AngleXU=0 Radius=170 StartAngle=0 EndAngle=0.966832
    g1: ArcOfCircle CenterX=0 CenterY=0 CenterZ=0 NormalX=0 NormalY=0 NormalZ=1 AngleXU=0 Radius=185 StartAngle=0 EndAngle=1.0335
    g2: LineSegment [constr] StartX=0 StartY=0 StartZ=0 EndX=91.2414 EndY=158.035 EndZ=0
    g3: ArcOfCircle CenterX=105.063 CenterY=152.272 CenterZ=0 NormalX=0 NormalY=0 NormalZ=1 AngleXU=0 Radius=15 StartAngle=2.77221 EndAngle=4.10842
    g4: ArcOfCircle CenterX=93.4065 CenterY=156.785 CenterZ=0 NormalX=0 NormalY=0 NormalZ=1 AngleXU=0 Radius=2.5 StartAngle=1.0335 EndAngle=2.77221
  constraints (15):
    c: Coincident(g0,g-1)
    c: PointOnObject(g0,g-1)
    c: Coincident(g1,g0)
    c: PointOnObject(g1,g-1)
    c: DistanceX(g0) = 170  'min_r'
    c: DistanceX(g0,g1) = 15
    c: Coincident(g2,g0)
    c: Angle(g2) = 1.0472
    c: DistanceX(g1) = 185  'max_r'
    c: Tangent(g1,g4) = -1.5708
    c: Tangent(g3,g4) = -1.5708
    c: Radius(g4) = 2.5
    c: PointOnObject(g3,g1)
    c: Tangent(g2,g4) = 1.5708
    c: Tangent(g3,g0) = 1.5708
FEATURE [Part::FeaturePython] PolarArray  # WARN: FeaturePython — macro-defined, semantics opaque (R4)
  Alignment = 0
  AttacherType = Attacher::AttachEngine3D
  CellStart = A1
  Count = 4
  DistributionLaw = 0
  EndInclusive = true
  ExposePlacement = false
  FlipX = false
  FlipZ = false
  GeneratorMode = 0
  MarkerShape = 1
  MarkerSize = 0
  NumElements = 4
  OrientMode = 2
  Radius = 177
  Reverse = false
  SpanEnd = 55
  SpanStart = -55
  Step = 36.6667
  Type = lattice2PolarArray2.PolarArray
  UseArcRadius = false
  UseArcRange = 0
  VSGVersion = 1
  Values = -55.0 | -18.333333333333336 | 18.33333333333333 | 55.0
  ValuesSource = 2
  isLattice = 1
  expr: Radius = <<main_sketch>>.Constraints.min_r + 7 mm
  expr: SpanEnd = -SpanStart
FEATURE [Part::FeaturePython] Join  label="holes"  # WARN: FeaturePython — macro-defined, semantics opaque (R4)
  ExposePlacement = false
  Interleave = false
  Links = -> [PolarArray]
  MarkerShape = 1
  MarkerSize = 0
  NumElements = 4
  Type = lattice2JoinArrays.JoinArrays
  isLattice = 1
